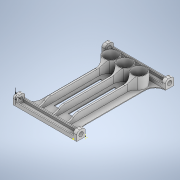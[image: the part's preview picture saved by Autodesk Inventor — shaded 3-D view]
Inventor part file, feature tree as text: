
AUTODESK INVENTOR PART (.ipt)
format: ipt  version: 2020 (Build 240168000, 168)  size: 716,800 bytes
history: native  units: mm
features: sketch x21, extrude x18, fillet x7
ambient origin geometry x8: Origin, YZ Plane, XZ Plane, XY Plane, X Axis, Y Axis, Z Axis, Center Point
bodies: Solid1 (feature_tree)
feature tree (46):
  extrude  "Extrusion1"  Depth=25.4mm
  extrude  "Extrusion2"  Depth=10.0mm TaperAngle=0.0deg
  sketch  "Sketch3"  dims[d5=2.0mm d6=190.0mm d7=0.0mm]
  extrude  "Extrusion3"  Depth=2.0mm TaperAngle=0.0deg
  extrude  "Extrusion4"  Depth=2.0mm
  fillet  "Fillet1"  Radius=8.75mm
  fillet  "Fillet2"  Radius=2.0mm
  sketch  "Sketch6"  dims[d16=2.0mm d17=290.0mm d18=0.0mm]
  extrude  "Extrusion5"  Depth=2.0mm
  sketch  "Sketch8"  dims[d22=10.0mm d23=0.0mm d24=10.0mm d25=0.0mm d26=8.75mm]
  extrude  "Extrusion6"  Depth=2.0mm TaperAngle=0.0deg
  extrude  "Extrusion7"  Depth=25.4mm
  fillet  "Fillet3"  Radius=12.7mm
  extrude  "Extrusion8"  Depth=10.0mm TaperAngle=0.0deg
  fillet  "Fillet4"  Radius=8.75mm
  extrude  "Extrusion9"  Depth=8.75mm TaperAngle=0.0deg
  extrude  "Extrusion10"  Depth=2.0mm
  extrude  "Extrusion11"  Depth=13.0mm
  extrude  "Extrusion12"  Depth=38.0mm
  extrude  "Extrusion13"  Depth=38.0mm
  fillet  "Fillet5"  Radius=30.0mm
  extrude  "Extrusion14"  Depth=35.0mm TaperAngle=0.0deg
  fillet  "Fillet6"  [1 undecoded]
  extrude  "Extrusion15"  TaperAngle=90.0deg  [1 undecoded]
  extrude  "Extrusion16"  Depth=2.0mm
  fillet  "Fillet7"  Radius=5.0mm
  extrude  "Extrusion17"  Depth=20.0mm TaperAngle=0.0deg
  extrude  "Extrusion18"  Depth=25.0mm TaperAngle=0.0deg
  sketch  "Sketch1"  dims[d0=25.4mm d1=25.4mm]
  sketch  "Sketch2"  dims[d2=12.7mm d3=10.0mm d4=0.0mm]
  sketch  "Sketch4"  dims[d8=10.0mm d9=0.0mm d10=5.0mm d11=8.75mm d12=0.0mm d13=2.0mm]
  sketch  "Sketch5"  dims[d14=8.75mm d15=2.0mm]
  sketch  "Sketch7"  dims[d19=25.4mm d20=25.4mm d21=12.7mm]
  sketch  "Sketch9"  dims[d27=5.0mm d28=8.75mm d29=0.0mm]
  sketch  "Sketch10"  dims[d30=2.0mm d31=13.0mm]
  sketch  "Sketch11"  dims[d32=190.0mm d33=0.0mm d34=13.0mm]
  sketch  "Sketch12"  dims[d35=190.0mm d36=0.0mm d37=38.0mm]
  sketch  "Sketch13"  dims[d38=38.0mm d39=38.0mm d40=30.0mm]
  sketch  "Sketch14"  dims[d41=30.0mm d42=35.0mm d43=0.0mm d44=90.0deg]
  sketch  "Sketch15"  dims[d45=90.0deg d46=90.0deg]
  sketch  "Sketch16"  dims[d47=2.0mm d48=0.0mm d49=5.0mm d50=5.0mm]
  sketch  "Sketch17"  dims[d51=5.0mm d52=20.0mm d53=0.0mm]
  sketch  "Sketch18"  dims[d54=25.0mm d55=89.0mm d56=0.0mm]
  sketch  "Sketch19"  dims[d57=25.0mm]
  sketch  "Sketch20"  dims[d58=37.0mm]
  sketch  "Sketch21"  dims[d59=37.0mm d60=20.0mm d61=0.0mm d62=5.0mm d63=5.0mm d64=8.75mm d65=0.0mm d66=2.0mm d67=38.55mm d68=38.55mm d69=38.55mm d70=35.0mm d71=0.0mm d72=17.0mm d73=17.0mm d74=2.0mm d75=0.0mm]
note: 2 required parameter values undecoded (feature->parameter linkage not recoverable at this tier; creation-order binding heuristic only, values carry confidence <= 0.55)
